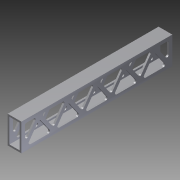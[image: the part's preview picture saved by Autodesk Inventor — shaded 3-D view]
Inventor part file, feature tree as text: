
AUTODESK INVENTOR PART (.ipt)
format: ipt  version: 2012 (Build 160160000, 160)  size: 291,328 bytes
history: native  units: in
note: dims shown in document units (in); Inventor stores cm internally (conversion verified against a paired STEP export)
features: extrude x2, sketch x2, fillet x1
ambient origin geometry x8: Origin, YZ Plane, XZ Plane, XY Plane, X Axis, Y Axis, Z Axis, Center Point
bodies: Solid1 (feature_tree)
feature tree (5):
  extrude  "Extrusion1"  Depth=1.0in
  extrude  "Extrusion2"  Depth=0.125in
  fillet  "Fillet1"  Radius=0.125in
  sketch  "Sketch1"  dims[d0=2.0in d1=1.0in]
  sketch  "Sketch2"  dims[d2=0.125in d3=0.125in d4=0.125in d5=0.125in d6=11.0in d7=0.0in d8=0.2404in d9=0.4809in d10=0.4809in d11=0.4809in d12=0.4809in d13=0.125in d14=0.125in d15=0.125in d16=0.125in d17=0.125in d18=0.125in d19=0.125in d20=0.125in d21=0.125in d22=0.125in d23=0.25in d24=0.25in d25=0.0in d26=0.25in d27=5.5in d28=1.0in d29=0.0in d30=0.125in]
